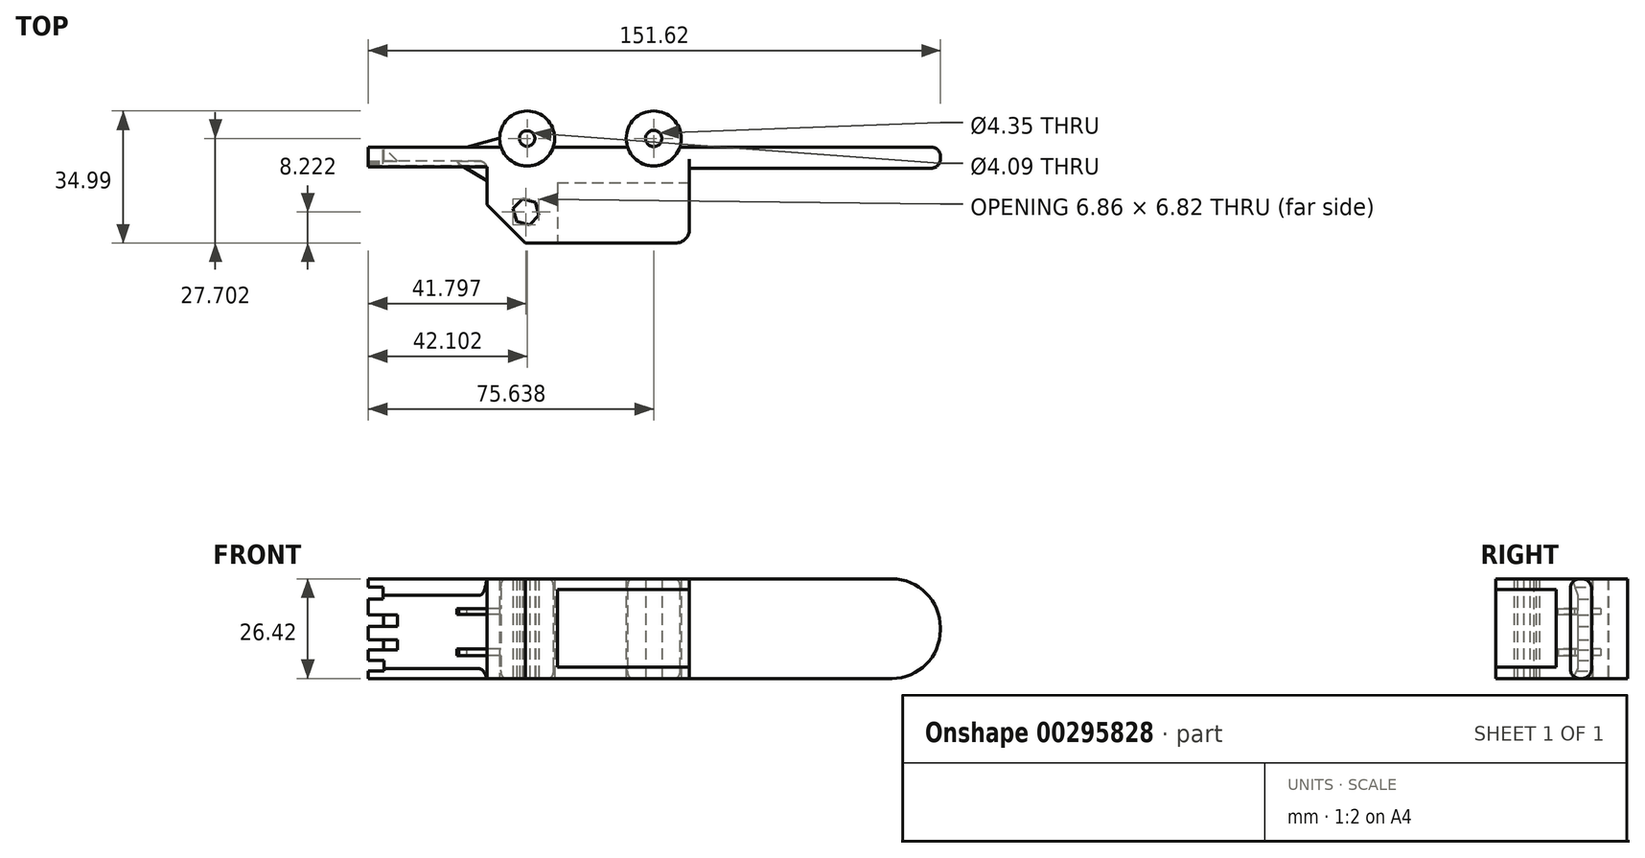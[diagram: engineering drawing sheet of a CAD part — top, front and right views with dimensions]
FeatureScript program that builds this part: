
annotation { "Feature Type Name" : "Feature", "Feature Type Description" : "" }
export const myFeature = defineFeature(function(context is Context, id is Id, definition is map)
    precondition{}
    {
        {
            var Q0;
            Q0=qCreatedBy(makeId("Front.planeOp"),FACE);
            var sketch = newSketch(context, id + "F0", { "sketchPlane" : qUnion([Q0])});
            skLineSegment(sketch, "E0.bottom", {"start": v(0, 0) * mm, "end": v(151.62, 0) * mm});
            skLineSegment(sketch, "E0.top", {"start": v(0, 26.38) * mm, "end": v(151.62, 26.38) * mm});
            skLineSegment(sketch, "E0.left", {"start": v(0, 0) * mm, "end": v(0, 26.38) * mm});
            skLineSegment(sketch, "E0.right", {"start": v(151.62, 0) * mm, "end": v(151.62, 26.38) * mm});
            skLineSegment(sketch, "E1", {"start": v(85.13, 26.38) * mm, "end": v(85.13, 0) * mm});
            skSolve(sketch);
        }
        {
            var Q0;
            {var subQ0=sQuery(id+"F0.wireOp",EDGE,"E0.left");Q0=makeQuery(id+"F0.imprint","IMPRINT",FACE,{"disambiguationData":[TD([[makeQuery(id+"F0.imprint","IMPRINT",EDGE,{"derivedFrom":subQ0}),-1.0]])]});}
            extrude(context, id + "F1", {"entities" : qUnion([Q0]), "depth" : 25.4 * mm});
        }
        {
            var Q0;
            {var subQ0=sQuery(id+"F0.wireOp",EDGE,"E0.right");Q0=makeQuery(id+"F0.imprint","IMPRINT",FACE,{"disambiguationData":[TD([[makeQuery(id+"F0.imprint","IMPRINT",EDGE,{"derivedFrom":subQ0}),1.0]])]});}
            extrude(context, id + "F2", {"entities" : qUnion([Q0]), "operationType" : NewBodyOperationType.ADD, "depth" : 5.6 * mm});
        }
        {
            var Q0;
            Q0=makeQuery(id+"F1.opExtrude","SWEPT_FACE",FACE,{"disambiguationData":[OSD([sQuery(id+"F0.wireOp",EDGE,"E0.left")])]});
            var sketch = newSketch(context, id + "F3", { "sketchPlane" : qUnion([Q0])});
            skLineSegment(sketch, "E2", {"start": v(7.62, 33.55) * mm, "end": v(3.69, 22) * mm});
            skLineSegment(sketch, "E3", {"start": v(3.69, 22) * mm, "end": v(3.69, 2.58) * mm});
            skLineSegment(sketch, "E4", {"start": v(3.69, 2.58) * mm, "end": v(7.87, -6.02) * mm});
            skLineSegment(sketch, "E5", {"start": v(7.87, -6.02) * mm, "end": v(35.64, -6.02) * mm});
            skLineSegment(sketch, "E6", {"start": v(35.64, -6.02) * mm, "end": v(35.64, 33.06) * mm});
            skLineSegment(sketch, "E7", {"start": v(35.64, 33.06) * mm, "end": v(7.62, 33.55) * mm});
            skSolve(sketch);
        }
        {
            var Q0;
            {var subQ0=sQuery(id+"F3.wireOp",EDGE,"E5");Q0=makeQuery(id+"F3.imprint","IMPRINT",FACE,{"disambiguationData":[TD([[makeQuery(id+"F3.imprint","IMPRINT",EDGE,{"derivedFrom":subQ0}),1.0]])]});}
            var Q1;
            {var subQ3=sQuery(id+"F3.wireOp",EDGE,"E3");Q1=makeQuery(id+"F3.imprint","IMPRINT",FACE,{"disambiguationData":[TD([[makeQuery(id+"F3.imprint","IMPRINT",EDGE,{"derivedFrom":subQ3}),1.0]])]});}
            extrude(context, id + "F4", {"entities" : qUnion([Q0, Q1]), "operationType" : NewBodyOperationType.REMOVE, "oppositeDirection" : true, "depth" : 31.5 * mm});
        }
        {
            var Q0;
            Q0=qCreatedBy(makeId("Front.planeOp"),FACE);
            var sketch = newSketch(context, id + "F5", { "sketchPlane" : qUnion([Q0])});
            skLineSegment(sketch, "E8.bottom", {"start": v(0, 24.19) * mm, "end": v(3.86, 24.19) * mm});
            skLineSegment(sketch, "E8.top", {"start": v(0, 21.03) * mm, "end": v(3.86, 21.03) * mm});
            skLineSegment(sketch, "E8.left", {"start": v(0, 24.19) * mm, "end": v(0, 21.03) * mm});
            skLineSegment(sketch, "E8.right", {"start": v(3.86, 24.19) * mm, "end": v(3.86, 21.03) * mm});
            skLineSegment(sketch, "E9.bottom", {"start": v(0, 16.87) * mm, "end": v(3.86, 16.87) * mm});
            skLineSegment(sketch, "E9.top", {"start": v(0, 13.84) * mm, "end": v(3.86, 13.84) * mm});
            skLineSegment(sketch, "E9.left", {"start": v(0, 16.87) * mm, "end": v(0, 13.84) * mm});
            skLineSegment(sketch, "E9.right", {"start": v(3.86, 16.87) * mm, "end": v(3.86, 13.84) * mm});
            skLineSegment(sketch, "E10.bottom", {"start": v(0, 10.3) * mm, "end": v(3.86, 10.3) * mm});
            skLineSegment(sketch, "E10.top", {"start": v(0, 7.53) * mm, "end": v(3.86, 7.53) * mm});
            skLineSegment(sketch, "E10.left", {"start": v(0, 10.3) * mm, "end": v(0, 7.53) * mm});
            skLineSegment(sketch, "E10.right", {"start": v(3.86, 10.3) * mm, "end": v(3.86, 7.53) * mm});
            skLineSegment(sketch, "E11.bottom", {"start": v(0, 4.76) * mm, "end": v(4.11, 4.76) * mm});
            skLineSegment(sketch, "E11.top", {"start": v(0, 1.98) * mm, "end": v(4.11, 1.98) * mm});
            skLineSegment(sketch, "E11.left", {"start": v(0, 4.76) * mm, "end": v(0, 1.98) * mm});
            skLineSegment(sketch, "E11.right", {"start": v(4.11, 4.76) * mm, "end": v(4.11, 1.98) * mm});
            skSolve(sketch);
        }
        {
            var Q0;
            Q0 = qSketchRegion(id + "F5", true);
            extrude(context, id + "F6", {"entities" : qUnion([Q0]), "operationType" : NewBodyOperationType.REMOVE, "depth" : 25.4 * mm});
        }
        {
            var Q0;
            Q0=qCreatedBy(makeId("Top.planeOp"),FACE);
            var sketch = newSketch(context, id + "F7", { "sketchPlane" : qUnion([Q0])});
            skCircle(sketch, "E12.cCircle", {"center": v(41.8, -17.18) * mm, "radius": 3.07 * mm, "construction": true});
            skLineSegment(sketch, "E12.0", {"start": v(38.37, -16.3) * mm, "end": v(40.84, -13.77) * mm});
            skLineSegment(sketch, "E12.1", {"start": v(40.84, -13.77) * mm, "end": v(44.27, -14.64) * mm});
            skLineSegment(sketch, "E12.2", {"start": v(44.27, -14.64) * mm, "end": v(45.23, -18.05) * mm});
            skLineSegment(sketch, "E12.3", {"start": v(45.23, -18.05) * mm, "end": v(42.75, -20.59) * mm});
            skLineSegment(sketch, "E12.4", {"start": v(42.75, -20.59) * mm, "end": v(39.32, -19.71) * mm});
            skLineSegment(sketch, "E12.5", {"start": v(39.32, -19.71) * mm, "end": v(38.37, -16.3) * mm});
            skPoint(sketch, "E12.0.midPoint", {"position": v(39.6, -15.04) * mm});
            skSolve(sketch);
        }
        {
            var Q0;
            Q0=makeQuery(id+"F7.imprint","IMPRINT",FACE,{"disambiguationData":[TD([[makeQuery(id+"F7.imprint","IMPRINT",EDGE,{"derivedFrom":sQuery(id+"F7.wireOp",EDGE,"E12.0")}),-1.0]])]});
            extrude(context, id + "F8", {"entities" : qUnion([Q0]), "operationType" : NewBodyOperationType.REMOVE, "depth" : 28.7 * mm});
        }
        {
            var Q0;
            Q0=makeQuery(id+"F4.boolean.opBoolean","INTERSECT",EDGE,{"derivedFrom":[makeQuery(id+"F1.opExtrude","CAP_FACE",FACE,{"disambiguationData":[OSD([sQuery(id+"F0.wireOp",EDGE,"E0.bottom"),sQuery(id+"F0.wireOp",EDGE,"E0.top"),sQuery(id+"F0.wireOp",EDGE,"E0.left"),sQuery(id+"F0.wireOp",EDGE,"E1")])],"isStart":false}),makeQuery(id+"F4.opExtrude","CAP_FACE",FACE,{"disambiguationData":[OSD([sQuery(id+"F3.wireOp",EDGE,"E2"),sQuery(id+"F3.wireOp",EDGE,"E3"),sQuery(id+"F3.wireOp",EDGE,"E4"),sQuery(id+"F3.wireOp",EDGE,"E5"),sQuery(id+"F3.wireOp",EDGE,"E6"),sQuery(id+"F3.wireOp",EDGE,"E7")])],"isStart":false})]});
            chamfer(context, id + "F9", {"entities" : qUnion([Q0]), "width" : 10.16 * mm, "tangentPropagation" : true});
        }
        {
            var Q0;
            Q0=makeQuery(id+"F1.opExtrude","CAP_EDGE",EDGE,{"disambiguationData":[OSD([sQuery(id+"F0.wireOp",EDGE,"E1")])],"isStart":false});
            fillet(context, id + "F10", {"entities" : qUnion([Q0]), "radius" : 3.68 * mm, "tangentPropagation" : true, "allowEdgeOverflow" : false});
        }
        {
            var Q0;
            Q0=makeQuery(id+"F4.boolean.opBoolean","COPY",EDGE,{"derivedFrom":makeQuery(id+"F4.opExtrude","CAP_EDGE",EDGE,{"disambiguationData":[OSD([sQuery(id+"F3.wireOp",EDGE,"E2")])],"isStart":true})});
            var Q1;
            {var subQ0=sQuery(id+"F3.wireOp",EDGE,"E3");Q1=makeQuery(id+"F6.boolean.opBoolean","SPLIT",EDGE,{"disambiguationData":[TD([makeQuery(id+"F6.opExtrude","SWEPT_FACE",FACE,{"disambiguationData":[OSD([sQuery(id+"F5.wireOp",EDGE,"E8.top")])]})])],"derivedFrom":makeQuery(id+"F4.boolean.opBoolean","COPY",EDGE,{"derivedFrom":makeQuery(id+"F4.opExtrude","CAP_EDGE",EDGE,{"disambiguationData":[OSD([subQ0])],"isStart":true})})});}
            var Q2;
            {var subQ0=sQuery(id+"F3.wireOp",EDGE,"E3");Q2=makeQuery(id+"F6.boolean.opBoolean","SPLIT",EDGE,{"disambiguationData":[TD([makeQuery(id+"F6.opExtrude","SWEPT_FACE",FACE,{"disambiguationData":[OSD([sQuery(id+"F5.wireOp",EDGE,"E9.top")])]})])],"derivedFrom":makeQuery(id+"F4.boolean.opBoolean","COPY",EDGE,{"derivedFrom":makeQuery(id+"F4.opExtrude","CAP_EDGE",EDGE,{"disambiguationData":[OSD([subQ0])],"isStart":true})})});}
            var Q3;
            {var subQ0=sQuery(id+"F3.wireOp",EDGE,"E3");Q3=makeQuery(id+"F6.boolean.opBoolean","SPLIT",EDGE,{"disambiguationData":[TD([makeQuery(id+"F6.opExtrude","SWEPT_FACE",FACE,{"disambiguationData":[OSD([sQuery(id+"F5.wireOp",EDGE,"E10.top")])]})])],"derivedFrom":makeQuery(id+"F4.boolean.opBoolean","COPY",EDGE,{"derivedFrom":makeQuery(id+"F4.opExtrude","CAP_EDGE",EDGE,{"disambiguationData":[OSD([subQ0])],"isStart":true})})});}
            var Q4;
            Q4=makeQuery(id+"F4.boolean.opBoolean","COPY",EDGE,{"derivedFrom":makeQuery(id+"F4.opExtrude","CAP_EDGE",EDGE,{"disambiguationData":[OSD([sQuery(id+"F3.wireOp",EDGE,"E4")])],"isStart":true})});
            var Q5;
            Q5=makeQuery(id+"F6.boolean.opBoolean","INTERSECT",EDGE,{"derivedFrom":[makeQuery(id+"F4.boolean.opBoolean","COPY",FACE,{"derivedFrom":makeQuery(id+"F4.opExtrude","SWEPT_FACE",FACE,{"disambiguationData":[OSD([sQuery(id+"F3.wireOp",EDGE,"E3")])]})}),makeQuery(id+"F6.opExtrude","SWEPT_FACE",FACE,{"disambiguationData":[OSD([sQuery(id+"F5.wireOp",EDGE,"E9.right")])]})]});
            var Q6;
            Q6=makeQuery(id+"F6.boolean.opBoolean","INTERSECT",EDGE,{"derivedFrom":[makeQuery(id+"F4.boolean.opBoolean","COPY",FACE,{"derivedFrom":makeQuery(id+"F4.opExtrude","SWEPT_FACE",FACE,{"disambiguationData":[OSD([sQuery(id+"F3.wireOp",EDGE,"E3")])]})}),makeQuery(id+"F6.opExtrude","SWEPT_FACE",FACE,{"disambiguationData":[OSD([sQuery(id+"F5.wireOp",EDGE,"E10.right")])]})]});
            chamfer(context, id + "F11", {"entities" : qUnion([Q0, Q1, Q2, Q3, Q4, Q5, Q6]), "width" : 3.8 * mm, "tangentPropagation" : true});
        }
        {
            var Q0;
            Q0=makeQuery(id+"F2.opExtrude","SWEPT_EDGE",EDGE,{"disambiguationData":[OSD([sQuery(id+"F0.wireOp",EDGE,"E0.bottom"),sQuery(id+"F0.wireOp",EDGE,"E0.right")])]});
            var Q1;
            Q1=makeQuery(id+"F2.opExtrude","SWEPT_EDGE",EDGE,{"disambiguationData":[OSD([sQuery(id+"F0.wireOp",EDGE,"E0.top"),sQuery(id+"F0.wireOp",EDGE,"E0.right")])]});
            fillet(context, id + "F12", {"entities" : qUnion([Q0, Q1]), "radius" : 12.88 * mm, "tangentPropagation" : true, "allowEdgeOverflow" : false});
        }
        {
            var Q0;
            Q0=makeQuery(id+"F1.opExtrude","CAP_FACE",FACE,{"disambiguationData":[OSD([sQuery(id+"F0.wireOp",EDGE,"E0.bottom"),sQuery(id+"F0.wireOp",EDGE,"E0.top"),sQuery(id+"F0.wireOp",EDGE,"E0.left"),sQuery(id+"F0.wireOp",EDGE,"E1")])],"isStart":false});
            var sketch = newSketch(context, id + "F13", { "sketchPlane" : qUnion([Q0])});
            skLineSegment(sketch, "E13.bottom", {"start": v(50.12, 23.52) * mm, "end": v(86.73, 23.52) * mm});
            skLineSegment(sketch, "E13.top", {"start": v(50.12, 3.02) * mm, "end": v(86.73, 3.02) * mm});
            skLineSegment(sketch, "E13.left", {"start": v(50.12, 23.52) * mm, "end": v(50.12, 3.02) * mm});
            skLineSegment(sketch, "E13.right", {"start": v(86.73, 23.52) * mm, "end": v(86.73, 3.02) * mm});
            skSolve(sketch);
        }
        {
            var Q0;
            Q0 = qSketchRegion(id + "F13", true);
            extrude(context, id + "F14", {"entities" : qUnion([Q0]), "operationType" : NewBodyOperationType.REMOVE, "oppositeDirection" : true, "depth" : 16 * mm});
        }
        {
            var Q0;
            {var subQ0=sQuery(id+"F0.wireOp",EDGE,"E0.bottom");Q0=makeQuery(id+"F2.boolean.opBoolean","MERGE",FACE,{"derivedFrom":[makeQuery(id+"F1.opExtrude","SWEPT_FACE",FACE,{"disambiguationData":[OSD([subQ0])]}),makeQuery(id+"F2.opExtrude","SWEPT_FACE",FACE,{"disambiguationData":[OSD([subQ0])]})]});}
            var sketch = newSketch(context, id + "F15", { "sketchPlane" : qUnion([Q0])});
            skCircle(sketch, "E14", {"center": v(42.1, -2.3) * mm, "radius": 7.29 * mm});
            skCircle(sketch, "E15", {"center": v(75.64, -2.3) * mm, "radius": 7.29 * mm});
            skCircle(sketch, "E16", {"center": v(42.1, -2.3) * mm, "radius": 2.04 * mm});
            skCircle(sketch, "E17", {"center": v(75.64, -2.3) * mm, "radius": 2.17 * mm});
            skSolve(sketch);
        }
        {
            var Q0;
            Q0 = qSketchRegion(id + "F15", true);
            extrude(context, id + "F16", {"entities" : qUnion([Q0]), "operationType" : NewBodyOperationType.ADD, "oppositeDirection" : true, "depth" : 26.42 * mm});
        }
        {
            var Q0;
            Q0=makeQuery(id+"F2.opExtrude","CAP_EDGE",EDGE,{"disambiguationData":[OSD([sQuery(id+"F0.wireOp",EDGE,"E0.bottom")])],"isStart":false});
            var Q1;
            {var subQ0=sQuery(id+"F0.wireOp",EDGE,"E1");var subQ1=sQuery(id+"F0.wireOp",EDGE,"E0.right");var subQ2=sQuery(id+"F0.wireOp",EDGE,"E0.top");var subQ3=sQuery(id+"F0.wireOp",EDGE,"E0.bottom");var subQ4=sQuery(id+"F15.wireOp",EDGE,"E15");Q1=makeQuery(id+"F16.boolean.opBoolean","SPLIT",EDGE,{"disambiguationData":[TD([makeQuery(id+"F1.opExtrude","SWEPT_FACE",FACE,{"disambiguationData":[OSD([subQ3])]}),makeQuery(id+"F1.opExtrude","CAP_FACE",FACE,{"disambiguationData":[OSD([subQ3,subQ2,sQuery(id+"F0.wireOp",EDGE,"E0.left"),subQ0])],"isStart":true}),makeQuery(id+"F2.opExtrude","SWEPT_FACE",FACE,{"disambiguationData":[OSD([subQ3])]}),makeQuery(id+"F2.opExtrude","CAP_FACE",FACE,{"disambiguationData":[OSD([subQ3,subQ2,subQ1,subQ0])],"isStart":true}),makeQuery(id+"F12.opFillet","BLEND_FACE",FACE,{"disambiguationData":[OSD([subQ3,subQ1])]}),makeQuery(id+"F16.opExtrude","CAP_FACE",FACE,{"disambiguationData":[OSD([sQuery(id+"F15.wireOp",EDGE,"E14"),sQuery(id+"F15.wireOp",EDGE,"E16")])],"isStart":true}),makeQuery(id+"F16.opExtrude","SWEPT_FACE",FACE,{"disambiguationData":[OSD([subQ4])]}),makeQuery(id+"F16.opExtrude","CAP_FACE",FACE,{"disambiguationData":[OSD([subQ4,sQuery(id+"F15.wireOp",EDGE,"E17")])],"isStart":true})])],"derivedFrom":makeQuery(id+"F2.boolean.opBoolean","MERGE",EDGE,{"derivedFrom":[makeQuery(id+"F1.opExtrude","CAP_EDGE",EDGE,{"disambiguationData":[OSD([subQ3])],"isStart":true}),makeQuery(id+"F2.opExtrude","CAP_EDGE",EDGE,{"disambiguationData":[OSD([subQ3])],"isStart":true})]})});}
            var Q2;
            {var subQ0=sQuery(id+"F0.wireOp",EDGE,"E1");var subQ1=sQuery(id+"F0.wireOp",EDGE,"E0.top");var subQ2=sQuery(id+"F0.wireOp",EDGE,"E0.bottom");var subQ3=sQuery(id+"F15.wireOp",EDGE,"E15");var subQ4=sQuery(id+"F15.wireOp",EDGE,"E14");Q2=makeQuery(id+"F16.boolean.opBoolean","SPLIT",EDGE,{"disambiguationData":[TD([makeQuery(id+"F1.opExtrude","SWEPT_FACE",FACE,{"disambiguationData":[OSD([subQ2])]}),makeQuery(id+"F1.opExtrude","CAP_FACE",FACE,{"disambiguationData":[OSD([subQ2,subQ1,sQuery(id+"F0.wireOp",EDGE,"E0.left"),subQ0])],"isStart":true}),makeQuery(id+"F2.opExtrude","SWEPT_FACE",FACE,{"disambiguationData":[OSD([subQ2])]}),makeQuery(id+"F2.opExtrude","CAP_FACE",FACE,{"disambiguationData":[OSD([subQ2,subQ1,sQuery(id+"F0.wireOp",EDGE,"E0.right"),subQ0])],"isStart":true}),makeQuery(id+"F16.opExtrude","SWEPT_FACE",FACE,{"disambiguationData":[OSD([subQ4])]}),makeQuery(id+"F16.opExtrude","CAP_FACE",FACE,{"disambiguationData":[OSD([subQ4,sQuery(id+"F15.wireOp",EDGE,"E16")])],"isStart":true}),makeQuery(id+"F16.opExtrude","SWEPT_FACE",FACE,{"disambiguationData":[OSD([subQ3])]}),makeQuery(id+"F16.opExtrude","CAP_FACE",FACE,{"disambiguationData":[OSD([subQ3,sQuery(id+"F15.wireOp",EDGE,"E17")])],"isStart":true})])],"derivedFrom":makeQuery(id+"F2.boolean.opBoolean","MERGE",EDGE,{"derivedFrom":[makeQuery(id+"F1.opExtrude","CAP_EDGE",EDGE,{"disambiguationData":[OSD([subQ2])],"isStart":true}),makeQuery(id+"F2.opExtrude","CAP_EDGE",EDGE,{"disambiguationData":[OSD([subQ2])],"isStart":true})]})});}
            var Q3;
            {var subQ0=sQuery(id+"F0.wireOp",EDGE,"E0.left");var subQ1=sQuery(id+"F0.wireOp",EDGE,"E0.bottom");var subQ2=sQuery(id+"F0.wireOp",EDGE,"E1");var subQ3=sQuery(id+"F0.wireOp",EDGE,"E0.top");var subQ4=sQuery(id+"F15.wireOp",EDGE,"E14");Q3=makeQuery(id+"F16.boolean.opBoolean","SPLIT",EDGE,{"disambiguationData":[TD([makeQuery(id+"F1.opExtrude","SWEPT_FACE",FACE,{"disambiguationData":[OSD([subQ1])]}),makeQuery(id+"F1.opExtrude","CAP_FACE",FACE,{"disambiguationData":[OSD([subQ1,subQ3,subQ0,subQ2])],"isStart":true}),makeQuery(id+"F1.opExtrude","SWEPT_FACE",FACE,{"disambiguationData":[OSD([subQ0])]}),makeQuery(id+"F2.opExtrude","SWEPT_FACE",FACE,{"disambiguationData":[OSD([subQ1])]}),makeQuery(id+"F2.opExtrude","CAP_FACE",FACE,{"disambiguationData":[OSD([subQ1,subQ3,sQuery(id+"F0.wireOp",EDGE,"E0.right"),subQ2])],"isStart":true}),makeQuery(id+"F16.opExtrude","SWEPT_FACE",FACE,{"disambiguationData":[OSD([subQ4])]}),makeQuery(id+"F16.opExtrude","CAP_FACE",FACE,{"disambiguationData":[OSD([subQ4,sQuery(id+"F15.wireOp",EDGE,"E16")])],"isStart":true}),makeQuery(id+"F16.opExtrude","CAP_FACE",FACE,{"disambiguationData":[OSD([sQuery(id+"F15.wireOp",EDGE,"E15"),sQuery(id+"F15.wireOp",EDGE,"E17")])],"isStart":true})])],"derivedFrom":makeQuery(id+"F2.boolean.opBoolean","MERGE",EDGE,{"derivedFrom":[makeQuery(id+"F1.opExtrude","CAP_EDGE",EDGE,{"disambiguationData":[OSD([subQ1])],"isStart":true}),makeQuery(id+"F2.opExtrude","CAP_EDGE",EDGE,{"disambiguationData":[OSD([subQ1])],"isStart":true})]})});}
            var Q4;
            {var subQ0=sQuery(id+"F0.wireOp",EDGE,"E0.top");var subQ1=sQuery(id+"F0.wireOp",EDGE,"E1");var subQ2=sQuery(id+"F0.wireOp",EDGE,"E0.bottom");Q4=makeQuery(id+"F16.boolean.opBoolean","SPLIT",EDGE,{"disambiguationData":[TD([makeQuery(id+"F1.opExtrude","CAP_FACE",FACE,{"disambiguationData":[OSD([subQ2,subQ0,sQuery(id+"F0.wireOp",EDGE,"E0.left"),subQ1])],"isStart":true}),makeQuery(id+"F1.opExtrude","SWEPT_FACE",FACE,{"disambiguationData":[OSD([subQ0])]}),makeQuery(id+"F2.opExtrude","CAP_FACE",FACE,{"disambiguationData":[OSD([subQ2,subQ0,sQuery(id+"F0.wireOp",EDGE,"E0.right"),subQ1])],"isStart":true}),makeQuery(id+"F2.opExtrude","SWEPT_FACE",FACE,{"disambiguationData":[OSD([subQ0])]}),makeQuery(id+"F16.opExtrude","SWEPT_FACE",FACE,{"disambiguationData":[OSD([sQuery(id+"F15.wireOp",EDGE,"E14")])]}),makeQuery(id+"F16.opExtrude","SWEPT_FACE",FACE,{"disambiguationData":[OSD([sQuery(id+"F15.wireOp",EDGE,"E15")])]})])],"derivedFrom":makeQuery(id+"F2.boolean.opBoolean","MERGE",EDGE,{"derivedFrom":[makeQuery(id+"F1.opExtrude","CAP_EDGE",EDGE,{"disambiguationData":[OSD([subQ0])],"isStart":true}),makeQuery(id+"F2.opExtrude","CAP_EDGE",EDGE,{"disambiguationData":[OSD([subQ0])],"isStart":true})]})});}
            var Q5;
            {var subQ0=sQuery(id+"F0.wireOp",EDGE,"E1");var subQ1=sQuery(id+"F0.wireOp",EDGE,"E0.top");var subQ2=sQuery(id+"F0.wireOp",EDGE,"E0.bottom");var subQ3=sQuery(id+"F0.wireOp",EDGE,"E0.left");Q5=makeQuery(id+"F16.boolean.opBoolean","SPLIT",EDGE,{"disambiguationData":[TD([makeQuery(id+"F1.opExtrude","CAP_FACE",FACE,{"disambiguationData":[OSD([subQ2,subQ1,subQ3,subQ0])],"isStart":true}),makeQuery(id+"F1.opExtrude","SWEPT_FACE",FACE,{"disambiguationData":[OSD([subQ1])]}),makeQuery(id+"F1.opExtrude","SWEPT_FACE",FACE,{"disambiguationData":[OSD([subQ3])]}),makeQuery(id+"F2.opExtrude","CAP_FACE",FACE,{"disambiguationData":[OSD([subQ2,subQ1,sQuery(id+"F0.wireOp",EDGE,"E0.right"),subQ0])],"isStart":true}),makeQuery(id+"F2.opExtrude","SWEPT_FACE",FACE,{"disambiguationData":[OSD([subQ1])]}),makeQuery(id+"F16.opExtrude","SWEPT_FACE",FACE,{"disambiguationData":[OSD([sQuery(id+"F15.wireOp",EDGE,"E14")])]})])],"derivedFrom":makeQuery(id+"F2.boolean.opBoolean","MERGE",EDGE,{"derivedFrom":[makeQuery(id+"F1.opExtrude","CAP_EDGE",EDGE,{"disambiguationData":[OSD([subQ1])],"isStart":true}),makeQuery(id+"F2.opExtrude","CAP_EDGE",EDGE,{"disambiguationData":[OSD([subQ1])],"isStart":true})]})});}
            fillet(context, id + "F17", {"entities" : qUnion([Q0, Q1, Q2, Q3, Q4, Q5]), "radius" : 2.45 * mm, "tangentPropagation" : true, "allowEdgeOverflow" : false});
        }
        {
            var Q0;
            Q0=qCreatedBy(makeId("Top.planeOp"),FACE);
            cPlane(context, id + "F18", {"entities" : qUnion([Q0]), "cplaneType" : CPlaneType.OFFSET, "offset" : 6.1 * mm, "width" : 152.4 * mm, "height" : 152.4 * mm});
        }
        {
            var Q0;
            Q0=qCreatedBy(makeId("Top.planeOp"),FACE);
            cPlane(context, id + "F19", {"entities" : qUnion([Q0]), "cplaneType" : CPlaneType.OFFSET, "offset" : 18.54 * mm, "width" : 152.4 * mm, "height" : 152.4 * mm});
        }
        {
            var Q0;
            Q0=qCreatedBy(id+"F18.planeOp",FACE);
            var sketch = newSketch(context, id + "F20", { "sketchPlane" : qUnion([Q0])});
            skLineSegment(sketch, "E18", {"start": v(24, -4.45) * mm, "end": v(32.83, -9.71) * mm});
            skLineSegment(sketch, "E19", {"start": v(32.83, -9.71) * mm, "end": v(38.62, 0) * mm});
            skLineSegment(sketch, "E20", {"start": v(38.62, 0) * mm, "end": v(36.49, 2.87) * mm});
            skLineSegment(sketch, "E21", {"start": v(36.49, 2.87) * mm, "end": v(21.68, -1.23) * mm});
            skLineSegment(sketch, "E22", {"start": v(21.68, -1.23) * mm, "end": v(24, -4.45) * mm});
            skSolve(sketch);
        }
        {
            var Q0;
            Q0 = qSketchRegion(id + "F20", true);
            extrude(context, id + "F21", {"entities" : qUnion([Q0]), "operationType" : NewBodyOperationType.ADD, "depth" : 1.78 * mm});
        }
        {
            var Q0;
            Q0=qCreatedBy(id+"F19.planeOp",FACE);
            var sketch = newSketch(context, id + "F22", { "sketchPlane" : qUnion([Q0])});
            skLineSegment(sketch, "E23", {"start": v(24.02, -4.4) * mm, "end": v(32.85, -9.66) * mm});
            skLineSegment(sketch, "E24", {"start": v(32.85, -9.66) * mm, "end": v(38.64, 0.05) * mm});
            skLineSegment(sketch, "E25", {"start": v(38.64, 0.05) * mm, "end": v(36.51, 2.92) * mm});
            skLineSegment(sketch, "E26", {"start": v(36.51, 2.92) * mm, "end": v(21.7, -1.18) * mm});
            skLineSegment(sketch, "E27", {"start": v(21.7, -1.18) * mm, "end": v(24.02, -4.4) * mm});
            skSolve(sketch);
        }
        {
            var Q0;
            Q0 = qSketchRegion(id + "F22", true);
            extrude(context, id + "F23", {"entities" : qUnion([Q0]), "operationType" : NewBodyOperationType.ADD, "oppositeDirection" : true, "depth" : 1.52 * mm});
        }
        {
            var Q0;
            {var subQ0=sQuery(id+"F3.wireOp",EDGE,"E3");var subQ1=sQuery(id+"F3.wireOp",EDGE,"E2");var subQ4=makeQuery(id+"F21.opExtrude","CAP_FACE",FACE,{"disambiguationData":[OSD([sQuery(id+"F20.wireOp",EDGE,"E18"),sQuery(id+"F20.wireOp",EDGE,"E19"),sQuery(id+"F20.wireOp",EDGE,"E20"),sQuery(id+"F20.wireOp",EDGE,"E21"),sQuery(id+"F20.wireOp",EDGE,"E22")])],"isStart":false});Q0=makeQuery(id+"F23.boolean.opBoolean","SPLIT",EDGE,{"disambiguationData":[TD([subQ4])],"derivedFrom":makeQuery(id+"F21.boolean.opBoolean","SPLIT",EDGE,{"disambiguationData":[TD([makeQuery(id+"F4.boolean.opBoolean","COPY",FACE,{"derivedFrom":makeQuery(id+"F4.opExtrude","SWEPT_FACE",FACE,{"disambiguationData":[OSD([subQ1])]})})])],"derivedFrom":makeQuery(id+"F4.boolean.opBoolean","COPY",EDGE,{"derivedFrom":makeQuery(id+"F4.opExtrude","CAP_EDGE",EDGE,{"disambiguationData":[OSD([subQ0])],"isStart":false})})})});}
            var Q1;
            {var subQ0=sQuery(id+"F3.wireOp",EDGE,"E4");var subQ1=sQuery(id+"F3.wireOp",EDGE,"E3");Q1=makeQuery(id+"F21.boolean.opBoolean","SPLIT",EDGE,{"disambiguationData":[TD([makeQuery(id+"F4.boolean.opBoolean","COPY",FACE,{"derivedFrom":makeQuery(id+"F4.opExtrude","SWEPT_FACE",FACE,{"disambiguationData":[OSD([subQ0])]})})])],"derivedFrom":makeQuery(id+"F4.boolean.opBoolean","COPY",EDGE,{"derivedFrom":makeQuery(id+"F4.opExtrude","CAP_EDGE",EDGE,{"disambiguationData":[OSD([subQ1])],"isStart":false})})});}
            var Q2;
            {var subQ0=sQuery(id+"F3.wireOp",EDGE,"E2");var subQ1=makeQuery(id+"F4.boolean.opBoolean","COPY",FACE,{"derivedFrom":makeQuery(id+"F4.opExtrude","SWEPT_FACE",FACE,{"disambiguationData":[OSD([subQ0])]})});var subQ2=sQuery(id+"F3.wireOp",EDGE,"E3");Q2=makeQuery(id+"F23.boolean.opBoolean","SPLIT",EDGE,{"disambiguationData":[TD([subQ1])],"derivedFrom":makeQuery(id+"F21.boolean.opBoolean","SPLIT",EDGE,{"disambiguationData":[TD([subQ1])],"derivedFrom":makeQuery(id+"F4.boolean.opBoolean","COPY",EDGE,{"derivedFrom":makeQuery(id+"F4.opExtrude","CAP_EDGE",EDGE,{"disambiguationData":[OSD([subQ2])],"isStart":false})})})});}
            fillet(context, id + "F24", {"entities" : qUnion([Q0, Q1, Q2]), "radius" : 2.08 * mm, "tangentPropagation" : true, "allowEdgeOverflow" : false});
        }
    });
